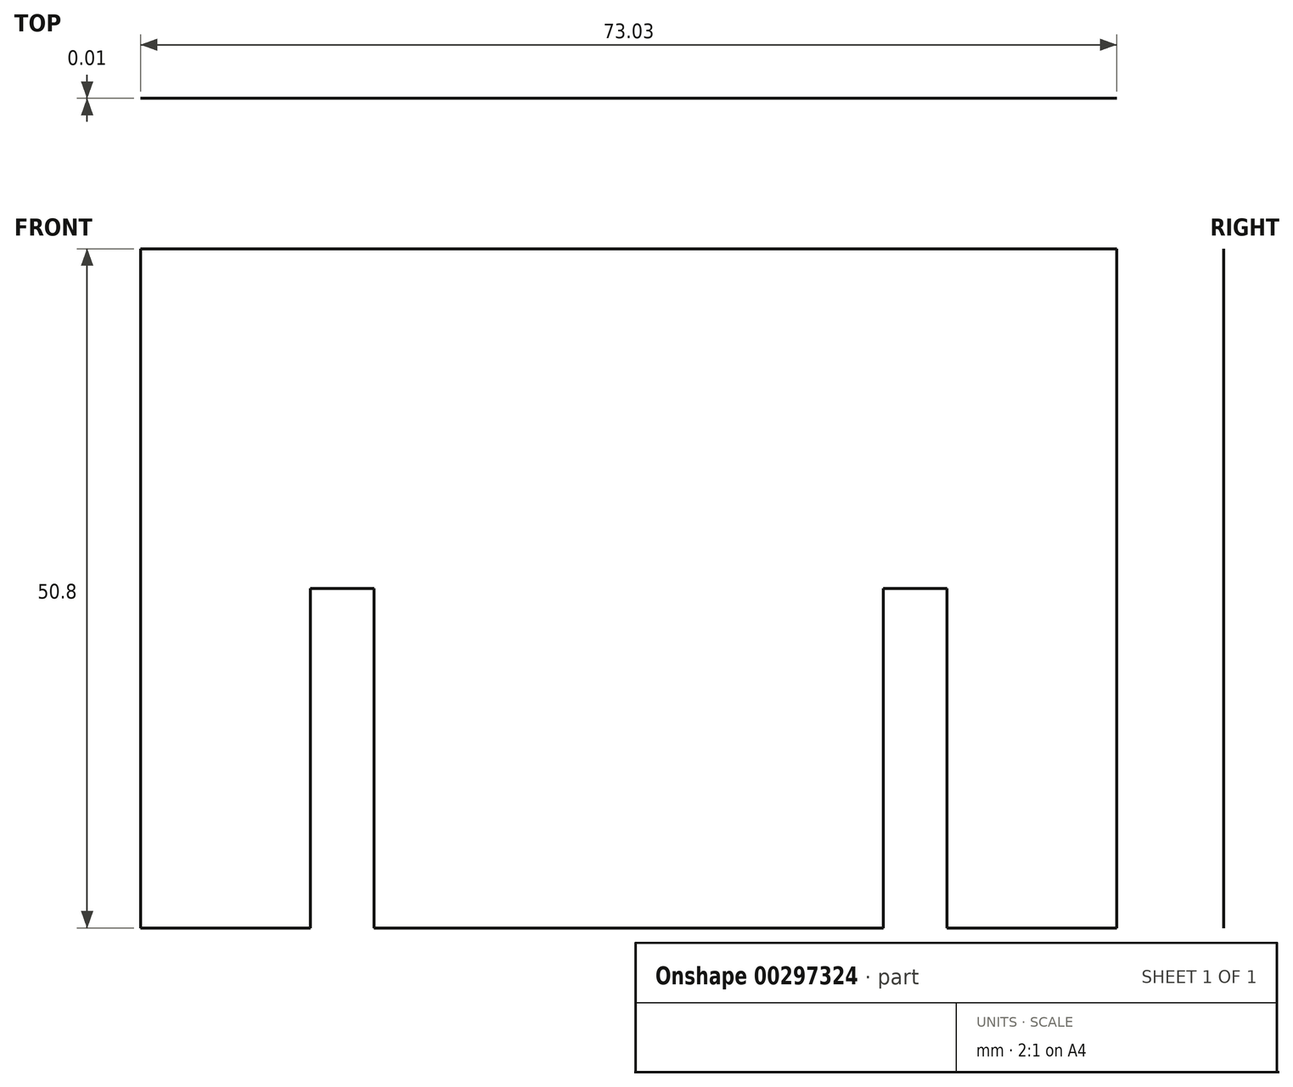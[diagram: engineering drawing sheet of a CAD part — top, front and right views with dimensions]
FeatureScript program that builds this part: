
annotation { "Feature Type Name" : "Feature", "Feature Type Description" : "" }
export const myFeature = defineFeature(function(context is Context, id is Id, definition is map)
    precondition{}
    {
        {
            var Q0;
            Q0=qCreatedBy(makeId("Front.planeOp"),FACE);
            var sketch = newSketch(context, id + "F0", { "sketchPlane" : qUnion([Q0])});
            skLineSegment(sketch, "E0", {"start": v(0, 0) * mm, "end": v(0, 50.8) * mm});
            skLineSegment(sketch, "E1", {"start": v(0, 50.8) * mm, "end": v(73.03, 50.8) * mm});
            skLineSegment(sketch, "E2", {"start": v(73.03, 50.8) * mm, "end": v(73.03, 0) * mm});
            skLineSegment(sketch, "E3", {"start": v(73.03, 0) * mm, "end": v(60.33, 0) * mm});
            skLineSegment(sketch, "E4", {"start": v(60.33, 0) * mm, "end": v(60.33, 25.4) * mm});
            skLineSegment(sketch, "E5", {"start": v(60.33, 25.4) * mm, "end": v(55.56, 25.4) * mm});
            skLineSegment(sketch, "E6", {"start": v(55.56, 25.4) * mm, "end": v(55.56, 0) * mm});
            skLineSegment(sketch, "E7", {"start": v(55.56, 0) * mm, "end": v(17.46, 0) * mm});
            skLineSegment(sketch, "E8", {"start": v(17.46, 0) * mm, "end": v(17.46, 25.4) * mm});
            skLineSegment(sketch, "E9", {"start": v(17.46, 25.4) * mm, "end": v(12.7, 25.4) * mm});
            skLineSegment(sketch, "E10", {"start": v(12.7, 25.4) * mm, "end": v(12.7, 0) * mm});
            skLineSegment(sketch, "E11", {"start": v(12.7, 0) * mm, "end": v(0, 0) * mm});
            skSolve(sketch);
        }
        {
            var Q0;
            Q0=makeQuery(id+"F0.imprint","IMPRINT",FACE,{"disambiguationData":[TD([[makeQuery(id+"F0.imprint","IMPRINT",EDGE,{"derivedFrom":sQuery(id+"F0.wireOp",EDGE,"E0")}),-1.0]])]});
            extrude(context, id + "F1", {"entities" : qUnion([Q0]), "depth" : 3 / 406.4 * mm});
        }
    });
